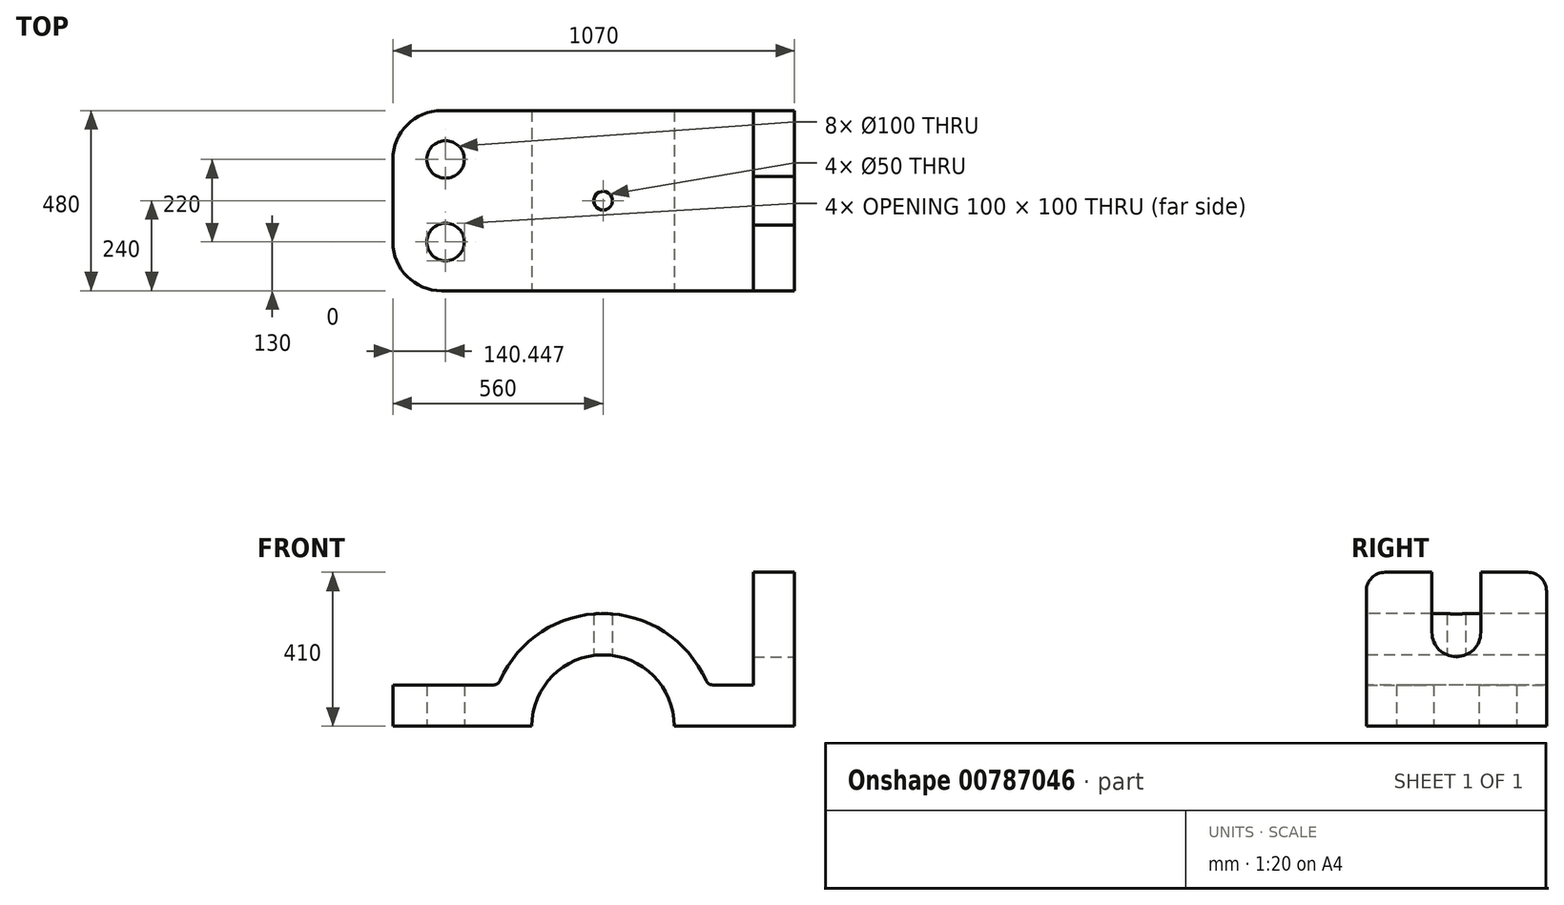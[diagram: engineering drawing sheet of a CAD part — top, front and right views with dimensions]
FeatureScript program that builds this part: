
annotation { "Feature Type Name" : "Feature", "Feature Type Description" : "" }
export const myFeature = defineFeature(function(context is Context, id is Id, definition is map)
    precondition{}
    {
        {
            var Q0;
            Q0=qCreatedBy(makeId("Front.planeOp"),FACE);
            var sketch = newSketch(context, id + "F0", { "sketchPlane" : qUnion([Q0])});
            skCircle(sketch, "E0", {"center": v(0, 0) * mm, "radius": 300 * mm});
            skCircle(sketch, "E1", {"center": v(0, 0) * mm, "radius": 190 * mm});
            skLineSegment(sketch, "E2.bottom", {"start": v(-560, 110) * mm, "end": v(510, 110) * mm});
            skLineSegment(sketch, "E2.top", {"start": v(-560, 0) * mm, "end": v(510, 0) * mm});
            skLineSegment(sketch, "E2.left", {"start": v(-560, 110) * mm, "end": v(-560, 0) * mm});
            skLineSegment(sketch, "E2.right", {"start": v(510, 110) * mm, "end": v(510, 0) * mm});
            skLineSegment(sketch, "E3.bottom", {"start": v(510, 110) * mm, "end": v(400, 110) * mm});
            skLineSegment(sketch, "E3.top", {"start": v(510, 410) * mm, "end": v(400, 410) * mm});
            skLineSegment(sketch, "E3.left", {"start": v(510, 110) * mm, "end": v(510, 410) * mm});
            skLineSegment(sketch, "E3.right", {"start": v(400, 110) * mm, "end": v(400, 410) * mm});
            skSolve(sketch);
        }
        {
            var Q0;
            {var subQ0=sQuery(id+"F0.wireOp",EDGE,"E2.bottom");var subQ1=sQuery(id+"F0.wireOp",EDGE,"E0");var subQ2=makeQuery(id+"F0.imprint","INTERSECT",VERTEX,{"disambiguationData":[OD(0.0)],"derivedFrom":[subQ1,subQ0]});Q0=makeQuery(id+"F0.imprint","IMPRINT",FACE,{"disambiguationData":[TD([[makeQuery(id+"F0.imprint","IMPRINT",EDGE,{"disambiguationData":[TD([[subQ2,-1.0]])],"derivedFrom":subQ1}),1.0]])]});}
            var Q1;
            {var subQ0=sQuery(id+"F0.wireOp",EDGE,"E2.top");var subQ1=sQuery(id+"F0.wireOp",EDGE,"E0");var subQ2=makeQuery(id+"F0.imprint","INTERSECT",VERTEX,{"disambiguationData":[OD(0.0)],"derivedFrom":[subQ1,subQ0]});Q1=makeQuery(id+"F0.imprint","IMPRINT",FACE,{"disambiguationData":[TD([[makeQuery(id+"F0.imprint","IMPRINT",EDGE,{"disambiguationData":[TD([[subQ2,-1.0]])],"derivedFrom":subQ1}),1.0]])]});}
            var Q2;
            {var subQ5=sQuery(id+"F0.wireOp",EDGE,"E2.left");Q2=makeQuery(id+"F0.imprint","IMPRINT",FACE,{"disambiguationData":[TD([[makeQuery(id+"F0.imprint","IMPRINT",EDGE,{"derivedFrom":subQ5}),1.0]])]});}
            var Q3;
            {var subQ0=sQuery(id+"F0.wireOp",EDGE,"E2.bottom");var subQ1=sQuery(id+"F0.wireOp",EDGE,"E0");var subQ2=makeQuery(id+"F0.imprint","INTERSECT",VERTEX,{"disambiguationData":[OD(1.0)],"derivedFrom":[subQ1,subQ0]});Q3=makeQuery(id+"F0.imprint","IMPRINT",FACE,{"disambiguationData":[TD([[makeQuery(id+"F0.imprint","IMPRINT",EDGE,{"disambiguationData":[TD([[subQ2,-1.0]])],"derivedFrom":subQ1}),1.0]])]});}
            var Q4;
            {var subQ3=sQuery(id+"F0.wireOp",EDGE,"E2.right");Q4=makeQuery(id+"F0.imprint","IMPRINT",FACE,{"disambiguationData":[TD([[makeQuery(id+"F0.imprint","IMPRINT",EDGE,{"derivedFrom":subQ3}),-1.0]])]});}
            var Q5;
            Q5=makeQuery(id+"F0.imprint","IMPRINT",FACE,{"disambiguationData":[TD([[makeQuery(id+"F0.imprint","IMPRINT",EDGE,{"derivedFrom":sQuery(id+"F0.wireOp",EDGE,"E3.top")}),1.0]])]});
            extrude(context, id + "F1", {"entities" : qUnion([Q0, Q1, Q2, Q3, Q4, Q5]), "endBound" : BoundingType.SYMMETRIC, "oppositeDirection" : true, "depth" : 480 * mm, "offsetDistance" : 25 * mm});
        }
        {
            var Q0;
            Q0=makeQuery(id+"F1.opExtrude","SWEPT_FACE",FACE,{"disambiguationData":[OSD([sQuery(id+"F0.wireOp",EDGE,"E2.right"),sQuery(id+"F0.wireOp",EDGE,"E3.left")])]});
            var sketch = newSketch(context, id + "F2", { "sketchPlane" : qUnion([Q0])});
            skLineSegment(sketch, "E4", {"start": v(0, 0) * mm, "end": v(0, 14.13) * mm, "construction": true});
            skLineSegment(sketch, "E5", {"start": v(0, 410) * mm, "end": v(0, 0) * mm, "construction": true});
            skCircle(sketch, "E6", {"center": v(0, 250) * mm, "radius": 65 * mm});
            skLineSegment(sketch, "E7", {"start": v(-65, 250) * mm, "end": v(-65, 410) * mm});
            skLineSegment(sketch, "E8", {"start": v(65, 250) * mm, "end": v(65, 410) * mm});
            skSolve(sketch);
        }
        {
            var Q0;
            {var subQ0=sQuery(id+"F2.wireOp",EDGE,"E6");var subQ1=makeQuery(id+"F2.imprint","INTERSECT",VERTEX,{"derivedFrom":[subQ0,sQuery(id+"F2.wireOp",EDGE,"E7")]});Q0=makeQuery(id+"F2.imprint","IMPRINT",FACE,{"disambiguationData":[TD([[makeQuery(id+"F2.imprint","IMPRINT",EDGE,{"disambiguationData":[TD([[subQ1,1.0]])],"derivedFrom":subQ0}),1.0]])]});}
            var Q1;
            {var subQ0=sQuery(id+"F2.wireOp",EDGE,"E7");Q1=makeQuery(id+"F2.imprint","IMPRINT",FACE,{"disambiguationData":[TD([[makeQuery(id+"F2.imprint","IMPRINT",EDGE,{"derivedFrom":subQ0}),-1.0]])]});}
            var Q2;
            Q2=makeQuery(id+"F1.opExtrude","SWEPT_FACE",FACE,{"disambiguationData":[OSD([sQuery(id+"F0.wireOp",EDGE,"E3.right")])]});
            extrude(context, id + "F3", {"entities" : qUnion([Q0, Q1]), "operationType" : NewBodyOperationType.REMOVE, "endBound" : BoundingType.UP_TO_SURFACE, "oppositeDirection" : true, "depth" : 25 * mm, "endBoundEntityFace" : qUnion([Q2]), "offsetDistance" : 25 * mm});
        }
        {
            var Q0;
            Q0=qCreatedBy(makeId("Top.planeOp"),FACE);
            var sketch = newSketch(context, id + "F4", { "sketchPlane" : qUnion([Q0])});
            skCircle(sketch, "E9", {"center": v(0, 0) * mm, "radius": 25 * mm});
            skLineSegment(sketch, "E10", {"start": v(-419.55, -240) * mm, "end": v(-419.55, 240) * mm, "construction": true});
            skLineSegment(sketch, "E11", {"start": v(-560, 0) * mm, "end": v(-279.1, 0) * mm, "construction": true});
            skCircle(sketch, "E12", {"center": v(-419.55, 110) * mm, "radius": 50 * mm});
            skCircle(sketch, "E13", {"center": v(-419.55, -110) * mm, "radius": 50 * mm});
            skSolve(sketch);
        }
        {
            var Q0;
            Q0=makeQuery(id+"F4.imprint","IMPRINT",FACE,{"disambiguationData":[TD([[makeQuery(id+"F4.imprint","IMPRINT",EDGE,{"derivedFrom":sQuery(id+"F4.wireOp",EDGE,"E12")}),1.0]])]});
            var Q1;
            Q1=makeQuery(id+"F4.imprint","IMPRINT",FACE,{"disambiguationData":[TD([[makeQuery(id+"F4.imprint","IMPRINT",EDGE,{"derivedFrom":sQuery(id+"F4.wireOp",EDGE,"E13")}),1.0]])]});
            var Q2;
            Q2=makeQuery(id+"F4.imprint","IMPRINT",FACE,{"disambiguationData":[TD([[makeQuery(id+"F4.imprint","IMPRINT",EDGE,{"derivedFrom":sQuery(id+"F4.wireOp",EDGE,"E9")}),1.0]])]});
            extrude(context, id + "F5", {"entities" : qUnion([Q0, Q1, Q2]), "operationType" : NewBodyOperationType.REMOVE, "endBound" : BoundingType.THROUGH_ALL, "depth" : 25 * mm, "offsetDistance" : 25 * mm});
        }
        {
            var Q0;
            Q0=makeQuery(id+"F1.opExtrude","CAP_EDGE",EDGE,{"disambiguationData":[OSD([sQuery(id+"F0.wireOp",EDGE,"E2.left")])],"isStart":false});
            var Q1;
            Q1=makeQuery(id+"F1.opExtrude","CAP_EDGE",EDGE,{"disambiguationData":[OSD([sQuery(id+"F0.wireOp",EDGE,"E2.left")])],"isStart":true});
            fillet(context, id + "F6", {"entities" : qUnion([Q0, Q1]), "radius" : 130 * mm, "tangentPropagation" : true, "allowEdgeOverflow" : false});
        }
        {
            var Q0;
            Q0=makeQuery(id+"F1.opExtrude","CAP_EDGE",EDGE,{"disambiguationData":[OSD([sQuery(id+"F0.wireOp",EDGE,"E3.top")])],"isStart":false});
            var Q1;
            Q1=makeQuery(id+"F1.opExtrude","CAP_EDGE",EDGE,{"disambiguationData":[OSD([sQuery(id+"F0.wireOp",EDGE,"E3.top")])],"isStart":true});
            fillet(context, id + "F7", {"entities" : qUnion([Q0, Q1]), "radius" : 50 * mm, "tangentPropagation" : true, "allowEdgeOverflow" : false});
        }
        {
            var Q0;
            {var subQ0=sQuery(id+"F0.wireOp",EDGE,"E2.bottom");var subQ1=sQuery(id+"F0.wireOp",EDGE,"E0");Q0=makeQuery(id+"F1.opExtrude","SWEPT_EDGE",EDGE,{"disambiguationData":[OSD([subQ1,subQ0]),TDD([makeQuery(id+"F0.imprint","INTERSECT",VERTEX,{"disambiguationData":[OD(1.0)],"derivedFrom":[subQ1,subQ0]})])]});}
            var Q1;
            {var subQ0=sQuery(id+"F0.wireOp",EDGE,"E2.bottom");var subQ1=sQuery(id+"F0.wireOp",EDGE,"E0");Q1=makeQuery(id+"F1.opExtrude","SWEPT_EDGE",EDGE,{"disambiguationData":[OSD([subQ1,subQ0]),TDD([makeQuery(id+"F0.imprint","INTERSECT",VERTEX,{"disambiguationData":[OD(0.0)],"derivedFrom":[subQ1,subQ0]})])]});}
            fillet(context, id + "F8", {"entities" : qUnion([Q0, Q1]), "radius" : 20 * mm, "tangentPropagation" : true, "allowEdgeOverflow" : false});
        }
    });
